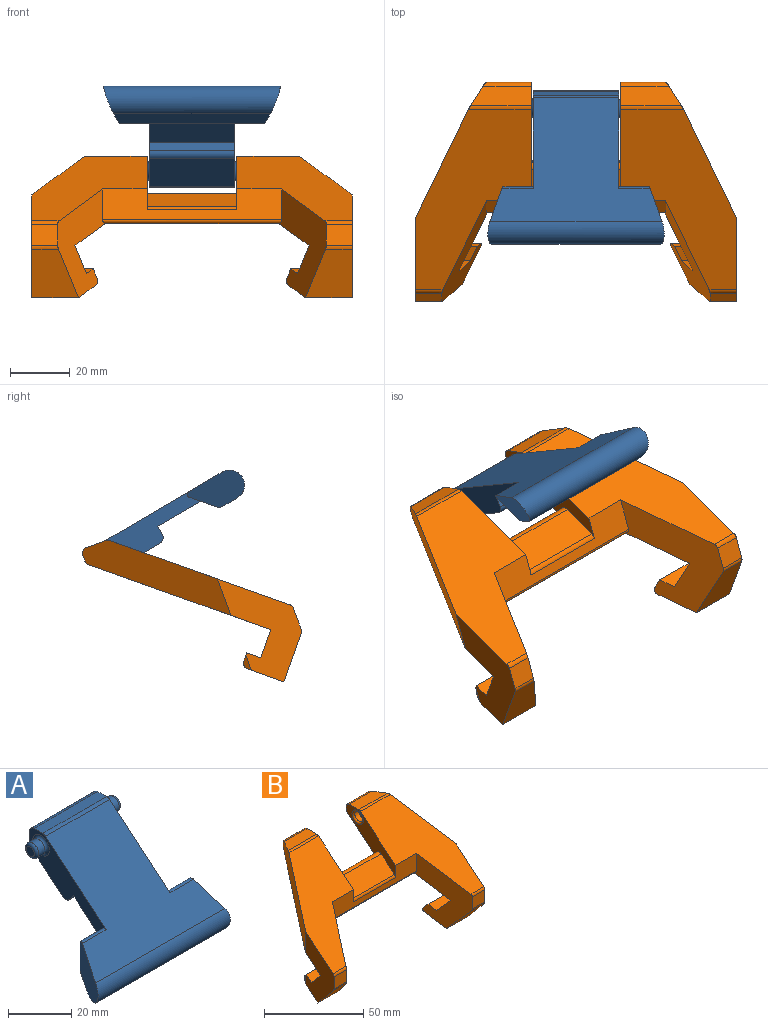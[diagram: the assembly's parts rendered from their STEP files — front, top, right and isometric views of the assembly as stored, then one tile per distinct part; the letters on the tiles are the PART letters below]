
ASSEMBLY  parts=2 mates=1
PART A: 28 faces, bbox 59.1x45.9x40.3 mm
  f0: cylinder r=2.75mm len=5.5mm, axis (-1,0,0), area 47.5mm2, adj f24,f27
  f1: plane 3.5x3.5mm, normal (1,0,0), area 9.6mm2, adj f27
  f2: plane 34.14x28mm, normal (1,0,0), area 262.6mm2, adj f6,f7,f8,f9,f10,f11,f12,f17
  f3: plane 17.43x13.4mm, normal (-0.93,0.37,0), area 159.2mm2, adj f4,f10,f12,f16,f18,f19
  f4: plane 52.55x4.83mm, normal (0,0.64,-0.77), area 318.9mm2, adj f3,f5,f16,f18
  f5: plane 17.43x13.4mm, normal (0.93,0.37,0), area 159.2mm2, adj f4,f10,f12,f16,f17,f18
  f6: plane 28.5x4.58mm, normal (0,1,0), area 130.7mm2, adj f2,f13,f20,f21
  f7: plane 28.5x3.87mm, normal (0,0,1), area 110.3mm2, adj f2,f13,f21,f22
  f8: plane 28.5x12.81mm, normal (0,0.64,-0.77), area 476.5mm2, adj f2,f9,f10,f13
  f9: plane 28.5x2.45mm, normal (0,-0.77,-0.64), area 91.2mm2, adj f2,f8,f13,f23
  f10: plane 48.4x10.44mm, normal (0,1,0), area 388mm2, adj f2,f3,f5,f8,f13,f17,f18,f19
  f11: plane 28.5x14.1mm, normal (0,0.64,-0.77), area 524.7mm2, adj f2,f13,f20,f23
  f12: plane 57.69x36.96mm, normal (0,-0.64,0.77), area 1702.8mm2, adj f2,f3,f5,f13,f16,f17,f19,f22
  f13: plane 34.14x28mm, normal (-1,0,0), area 262.6mm2, adj f6,f7,f8,f9,f10,f11,f12,f19
  f14: plane 3.5x3.5mm, normal (-1,0,0), area 9.6mm2, adj f26
  f15: cylinder r=2.75mm len=5.5mm, axis (-1,0,0), area 47.5mm2, adj f25,f26
  f16: cylinder r=5mm len=59.13mm, axis (-1,0,0), area 896.4mm2, adj f3,f4,f5,f12
  f17: cylinder r=1mm len=10.61mm, axis (1,0,0), area 23.2mm2, adj f2,f5,f10,f12
  f18: cylinder r=1mm len=48.69mm, axis (-1,0,0), area 42.3mm2, adj f3,f4,f5,f10
  f19: cylinder r=1mm len=10.61mm, axis (1,0,0), area 23.2mm2, adj f3,f10,f12,f13
  f20: cylinder r=2mm len=28.5mm, axis (1,0,0), area 49.7mm2, adj f2,f6,f11,f13
  f21: cylinder r=2mm len=28.5mm, axis (-1,0,0), area 89.5mm2, adj f2,f6,f7,f13
  f22: cylinder r=2mm len=28.5mm, axis (1,0,0), area 39.8mm2, adj f2,f7,f12,f13
  f23: cylinder r=2mm len=28.5mm, axis (-1,0,0), area 89.5mm2, adj f2,f9,f11,f13
  f24: torus R=3.75mm, axis (1,0,0), area 30.7mm2, adj f0,f2
  f25: torus R=3.75mm, axis (1,0,0), area 30.7mm2, adj f13,f15
  f26: torus R=1.75mm, axis (1,0,0), area 23.6mm2, adj f14,f15
  f27: torus R=1.75mm, axis (1,0,0), area 23.6mm2, adj f0,f1
PART B: 54 faces, bbox 107.5x60x65.2 mm
  f0: plane 49.13x41.22mm, normal (0,-0.64,0.77), area 1439.6mm2, adj f1,f18,f19,f20,f27,f36,f43
  f1: plane 60x10.91mm, normal (0,-1,0), area 430.8mm2, adj f0,f9,f20,f21,f27,f28,f50,f53
  f2: plane 5.37x1.83mm, normal (-0.86,0.51,0), area 7.3mm2, adj f10,f12,f18,f37
  f3: plane 15.69x13.23mm, normal (0,-0.77,-0.64), area 213.5mm2, adj f10,f18,f27,f35
  f4: plane 20.66x3.83mm, normal (0,-0.64,0.77), area 97.5mm2, adj f5,f12,f18,f27
  f5: plane 18.36x7.66mm, normal (0,0.77,0.64), area 164.3mm2, adj f4,f7,f18,f27
  f6: plane 40.06x20.42mm, normal (1,0,0), area 430.5mm2, adj f7,f9,f11,f13,f15,f16,f17,f23
  f7: plane 107.5x49.7mm, normal (0,0.64,-0.77), area 3455.8mm2, adj f5,f6,f17,f18,f19,f20,f21,f23
  f8: plane 20.32x6.87mm, normal (0,0,1), area 125.5mm2, adj f21,f23,f45,f46
  f9: plane 49.13x41.22mm, normal (0,-0.64,0.77), area 1439.6mm2, adj f1,f6,f21,f23,f28,f38,f46
  f10: plane 21.67x9.96mm, normal (0,0.64,-0.77), area 242.4mm2, adj f2,f3,f18,f27,f37
  f11: plane 21.67x9.96mm, normal (0,0.64,-0.77), area 242.4mm2, adj f6,f15,f25,f28,f40
  f12: plane 21.82x2.3mm, normal (0,0.77,0.64), area 62.8mm2, adj f2,f4,f18,f27,f37
  f13: plane 21.82x2.3mm, normal (0,0.77,0.64), area 62.8mm2, adj f6,f16,f25,f28,f40
  f14: plane 20.32x6.87mm, normal (0,0,1), area 125.5mm2, adj f19,f20,f42,f43
  f15: plane 15.69x13.23mm, normal (0,-0.77,-0.64), area 213.5mm2, adj f6,f11,f28,f39
  f16: plane 20.66x3.83mm, normal (0,-0.64,0.77), area 97.5mm2, adj f6,f13,f17,f28
  f17: plane 18.36x7.66mm, normal (0,0.77,0.64), area 164.3mm2, adj f6,f7,f16,f28
  f18: plane 40.06x20.42mm, normal (-1,0,0), area 430.5mm2, adj f0,f2,f3,f4,f5,f7,f10,f12
  f19: plane 39.58x38.21mm, normal (-0.86,0.51,0), area 556.3mm2, adj f0,f7,f14,f18,f22,f41,f42,f43
  f20: plane 35x28.77mm, normal (1,0,0), area 280.1mm2, adj f0,f1,f7,f14,f22,f30,f41,f42
  f21: plane 35x28.77mm, normal (-1,0,0), area 280.1mm2, adj f1,f7,f8,f9,f24,f30,f44,f45
  f22: plane 15x2.07mm, normal (0,1,0), area 31mm2, adj f19,f20,f41,f42
  f23: plane 39.58x38.21mm, normal (0.86,0.51,0), area 556.3mm2, adj f6,f7,f8,f9,f24,f44,f45,f46
  f24: plane 15x2.07mm, normal (0,1,0), area 31mm2, adj f21,f23,f44,f45
  f25: plane 5.37x1.83mm, normal (0.86,0.51,0), area 7.3mm2, adj f6,f11,f13,f40
  f26: plane 8.75x7.48mm, normal (0,-1,0), area 65.4mm2, adj f18,f27,f35,f36
  f27: plane 43.9x26.64mm, normal (0.86,-0.51,0), area 580.2mm2, adj f0,f1,f3,f4,f5,f7,f10,f12
  f28: plane 43.9x26.64mm, normal (-0.86,-0.51,0), area 580.2mm2, adj f1,f7,f9,f11,f13,f15,f16,f17
  f29: plane 8.75x7.48mm, normal (0,-1,0), area 65.4mm2, adj f6,f28,f38,f39
  f30: plane 30x0.77mm, normal (0,0.77,0.64), area 30mm2, adj f20,f21,f51,f52
  f31: plane 6.1x6.1mm, normal (-1,0,0), area 29.2mm2, adj f32
  f32: cylinder r=3.05mm len=6.1mm, axis (-1,0,0), area 57.5mm2, adj f31,f48
  f33: cylinder r=3.05mm len=6.1mm, axis (-1,0,0), area 57.5mm2, adj f34,f47
  f34: plane 6.1x6.1mm, normal (1,0,0), area 29.2mm2, adj f33
  f35: cylinder r=2mm len=9.03mm, axis (1,0,0), area 12.4mm2, adj f3,f18,f26,f27
  f36: cylinder r=2mm len=9.18mm, axis (-1,0,0), area 15.5mm2, adj f0,f18,f26,f27
  f37: cylinder r=2mm len=21.43mm, axis (-1,0,0), area 66mm2, adj f2,f10,f12,f27
  f38: cylinder r=2mm len=9.18mm, axis (1,0,0), area 15.5mm2, adj f6,f9,f28,f29
  f39: cylinder r=2mm len=9.03mm, axis (-1,0,0), area 12.4mm2, adj f6,f15,f28,f29
  f40: cylinder r=2mm len=21.43mm, axis (-1,0,0), area 66mm2, adj f11,f13,f25,f28
  f41: cylinder r=2mm len=15.43mm, axis (-1,0,0), area 26.4mm2, adj f7,f19,f20,f22
  f42: cylinder r=2mm len=16.2mm, axis (1,0,0), area 48.5mm2, adj f14,f19,f20,f22
  f43: cylinder r=2mm len=21.09mm, axis (1,0,0), area 28.9mm2, adj f0,f14,f19,f20
  f44: cylinder r=2mm len=15.43mm, axis (1,0,0), area 26.4mm2, adj f7,f21,f23,f24
  f45: cylinder r=2mm len=16.2mm, axis (-1,0,0), area 48.5mm2, adj f8,f21,f23,f24
  f46: cylinder r=2mm len=21.09mm, axis (1,0,0), area 28.9mm2, adj f8,f9,f21,f23
  f47: torus R=4.05mm, axis (1,0,0), area 33.7mm2, adj f20,f33
  f48: torus R=4.05mm, axis (1,0,0), area 33.7mm2, adj f21,f32
  f49: plane 30x9.54mm, normal (0,-0.64,0.77), area 373.6mm2, adj f20,f21,f50,f51
  f50: cylinder r=2mm len=30mm, axis (1,0,0), area 52.4mm2, adj f1,f20,f21,f49
  f51: cylinder r=2mm len=30mm, axis (1,0,0), area 94.2mm2, adj f20,f21,f30,f49
  f52: cylinder r=2mm len=30mm, axis (1,0,0), area 94.2mm2, adj f7,f20,f21,f30
  f53: cylinder r=1mm len=60mm, axis (1,0,0), area 134.3mm2, adj f1,f7,f27,f28
PLACE A rot(axis=(-1,0,0),70.4deg) t=(0,-24.69,83.38)mm
PLACE B rot(axis=(-1,0,0),20.4deg) t=(0,-16.25,12.36)mm
MATE revolute A.f0 <-> B.f32  axis (1,0,0) through (19,55.69,56.93)mm
